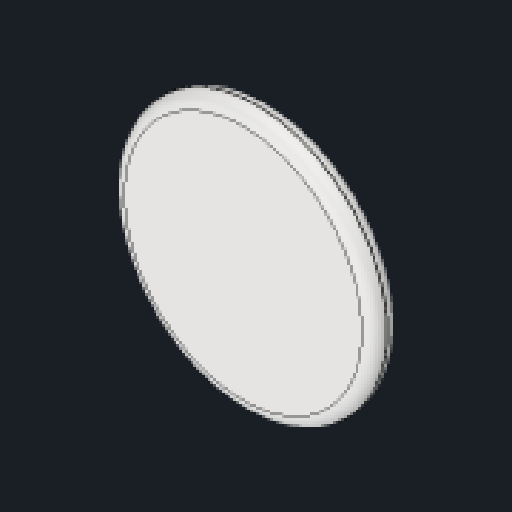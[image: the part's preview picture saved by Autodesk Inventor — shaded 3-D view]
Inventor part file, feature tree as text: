
AUTODESK INVENTOR PART (.ipt)
format: ipt  version: 2023.2 (Build 272271030, 271C)  size: 104,960 bytes
history: native  units: mm
features: extrude x1, fillet x1, sketch x1
ambient origin geometry x8: Origin, YZ Plane, XZ Plane, XY Plane, X Axis, Y Axis, Z Axis, Center Point
bodies: Solid1 (feature_tree)
feature tree (3):
  extrude  "Extrusion1"  Depth=3.5mm TaperAngle=0.0deg
  fillet  "Fillet1"  Radius=1.7mm
  sketch  "Sketch1"  dims[d0=36.0mm d1=3.5mm d2=0.0mm d3=1.7mm]
